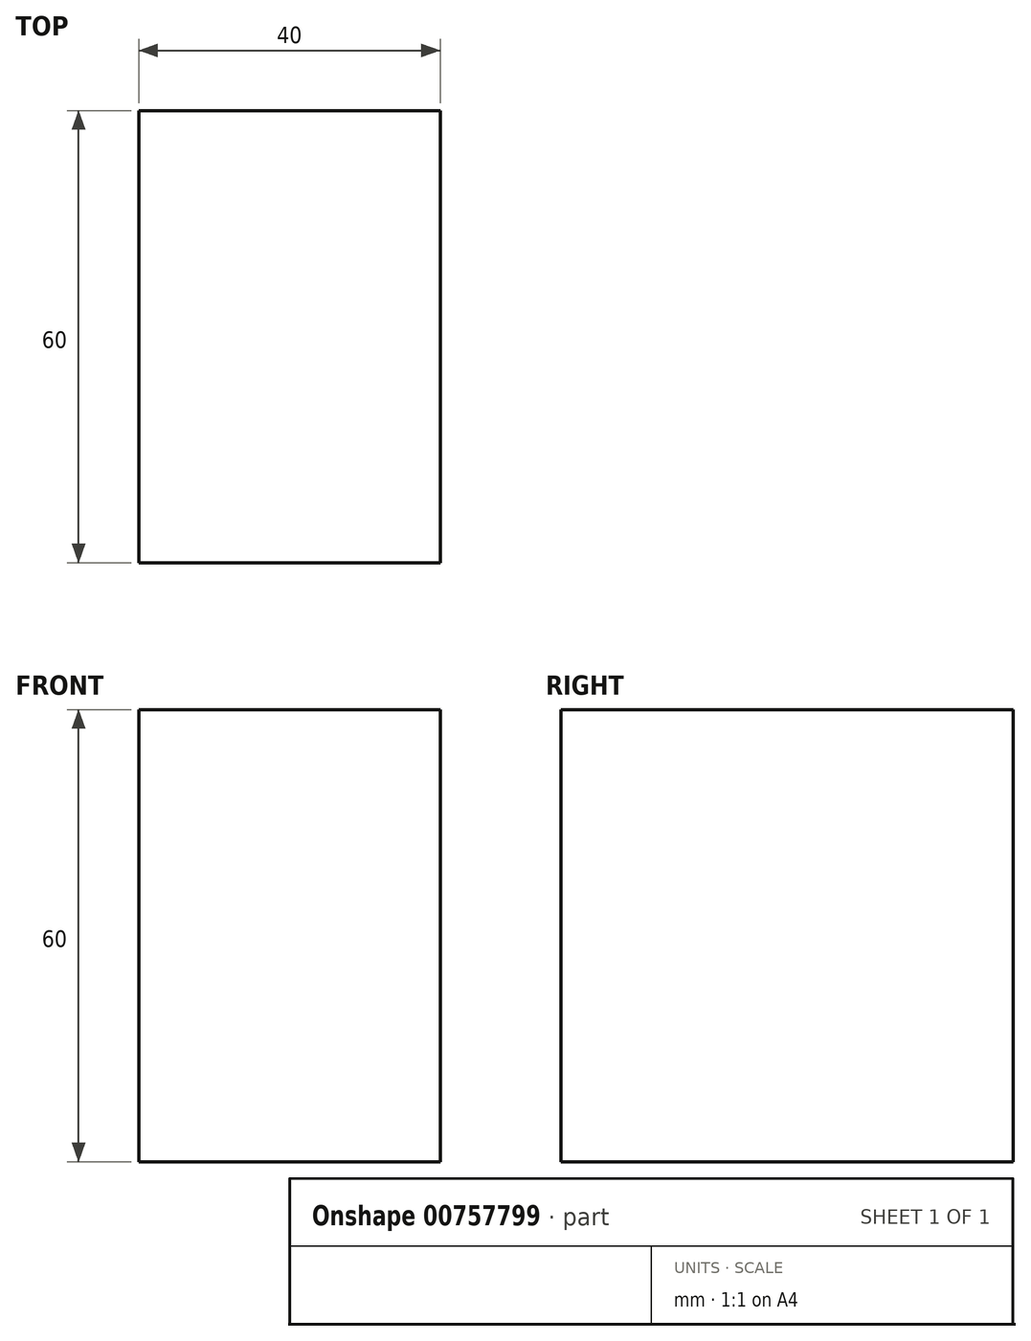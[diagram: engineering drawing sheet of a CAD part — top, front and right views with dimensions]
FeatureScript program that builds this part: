
annotation { "Feature Type Name" : "Feature", "Feature Type Description" : "" }
export const myFeature = defineFeature(function(context is Context, id is Id, definition is map)
    precondition{}
    {
        {
            var Q0;
            Q0=qCreatedBy(makeId("Top.planeOp"),FACE);
            var sketch = newSketch(context, id + "F0", { "sketchPlane" : qUnion([Q0])});
            skLineSegment(sketch, "E0", {"start": v(0, 0) * mm, "end": v(40, 0) * mm});
            skLineSegment(sketch, "E1", {"start": v(40, 0) * mm, "end": v(40, 60) * mm});
            skLineSegment(sketch, "E2", {"start": v(40, 60) * mm, "end": v(0, 60) * mm});
            skLineSegment(sketch, "E3", {"start": v(0, 60) * mm, "end": v(0, 0) * mm});
            skSolve(sketch);
        }
        {
            var Q0;
            Q0 = qSketchRegion(id + "F0", true);
            extrude(context, id + "F1", {"entities" : qUnion([Q0]), "depth" : 60 * mm, "offsetDistance" : 25 * mm});
        }
    });
